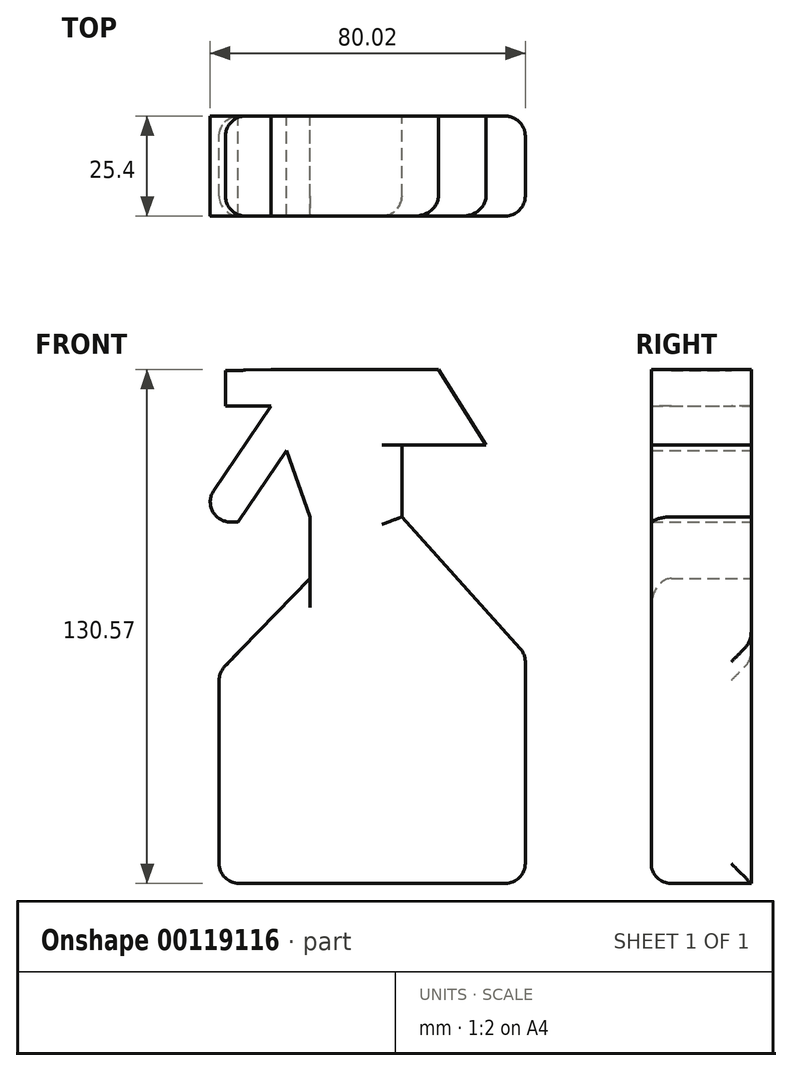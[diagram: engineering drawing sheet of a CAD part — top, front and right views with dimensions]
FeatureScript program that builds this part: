
annotation { "Feature Type Name" : "Feature", "Feature Type Description" : "" }
export const myFeature = defineFeature(function(context is Context, id is Id, definition is map)
    precondition{}
    {
        {
            var Q0;
            Q0=qCreatedBy(makeId("Front.planeOp"),FACE);
            var sketch = newSketch(context, id + "F0", { "sketchPlane" : qUnion([Q0])});
            skLineSegment(sketch, "E0", {"start": v(-54.09, 52.8) * mm, "end": v(-54.09, 43.84) * mm});
            skLineSegment(sketch, "E1", {"start": v(-54.09, 43.84) * mm, "end": v(-42.57, 43.84) * mm});
            skLineSegment(sketch, "E2", {"start": v(-42.57, 43.84) * mm, "end": v(-42.57, 53.12) * mm});
            skLineSegment(sketch, "E3", {"start": v(-54.09, 52.8) * mm, "end": v(-42.57, 53.12) * mm});
            skLineSegment(sketch, "E4", {"start": v(-42.57, 53.12) * mm, "end": v(0, 53.12) * mm});
            skLineSegment(sketch, "E5", {"start": v(0, 53.12) * mm, "end": v(12.11, 33.92) * mm});
            skLineSegment(sketch, "E6", {"start": v(12.11, 33.92) * mm, "end": v(-9.28, 33.92) * mm});
            skLineSegment(sketch, "E7", {"start": v(-9.28, 33.92) * mm, "end": v(-9.28, 15.68) * mm});
            skLineSegment(sketch, "E8", {"start": v(-9.28, 15.68) * mm, "end": v(-32.64, 15.68) * mm});
            skLineSegment(sketch, "E9", {"start": v(-32.64, 15.68) * mm, "end": v(-42.57, 43.84) * mm});
            skLineSegment(sketch, "E10", {"start": v(-42.57, 43.84) * mm, "end": v(-62.4, 14.4) * mm});
            skLineSegment(sketch, "E11", {"start": v(-62.4, 14.4) * mm, "end": v(-50.89, 14.4) * mm});
            skLineSegment(sketch, "E12", {"start": v(-50.89, 14.4) * mm, "end": v(-38.6, 32.6) * mm});
            skLineSegment(sketch, "E13", {"start": v(-32.64, 15.68) * mm, "end": v(-32.64, 0) * mm});
            skLineSegment(sketch, "E14", {"start": v(-32.64, 0) * mm, "end": v(-55.69, -23.8) * mm});
            skLineSegment(sketch, "E15", {"start": v(-55.69, -23.8) * mm, "end": v(-55.69, -77.45) * mm});
            skLineSegment(sketch, "E16", {"start": v(-55.69, -77.45) * mm, "end": v(22.08, -77.45) * mm});
            skLineSegment(sketch, "E17", {"start": v(22.08, -77.45) * mm, "end": v(22.08, -19.2) * mm});
            skLineSegment(sketch, "E18", {"start": v(-9.28, 15.68) * mm, "end": v(22.08, -19.2) * mm});
            skSolve(sketch);
        }
        {
            var Q0;
            Q0=makeQuery(id+"F0.imprint","IMPRINT",FACE,{"disambiguationData":[TD([[makeQuery(id+"F0.imprint","IMPRINT",EDGE,{"derivedFrom":sQuery(id+"F0.wireOp",EDGE,"E0")}),1.0]])]});
            var Q1;
            {var subQ0=sQuery(id+"F0.wireOp",EDGE,"E10");Q1=makeQuery(id+"F0.imprint","IMPRINT",FACE,{"disambiguationData":[TD([[makeQuery(id+"F0.imprint","IMPRINT",EDGE,{"derivedFrom":subQ0}),1.0]])]});}
            var Q2;
            Q2=makeQuery(id+"F0.imprint","IMPRINT",FACE,{"disambiguationData":[TD([[makeQuery(id+"F0.imprint","IMPRINT",EDGE,{"derivedFrom":sQuery(id+"F0.wireOp",EDGE,"E8")}),1.0]])]});
            var Q3;
            {var subQ0=sQuery(id+"F0.wireOp",EDGE,"E2");Q3=makeQuery(id+"F0.imprint","IMPRINT",FACE,{"disambiguationData":[TD([[makeQuery(id+"F0.imprint","IMPRINT",EDGE,{"derivedFrom":subQ0}),-1.0]])]});}
            extrude(context, id + "F1", {"entities" : qUnion([Q0, Q1, Q2, Q3]), "endBound" : BoundingType.SYMMETRIC, "depth" : 25.4 * mm});
        }
        {
            var Q0;
            Q0=makeQuery(id+"F1.opExtrude","CAP_EDGE",EDGE,{"disambiguationData":[OSD([sQuery(id+"F0.wireOp",EDGE,"E15")])],"isStart":false});
            var Q1;
            Q1=makeQuery(id+"F1.opExtrude","CAP_EDGE",EDGE,{"disambiguationData":[OSD([sQuery(id+"F0.wireOp",EDGE,"E14")])],"isStart":false});
            var Q2;
            Q2=makeQuery(id+"F1.opExtrude","SWEPT_EDGE",EDGE,{"disambiguationData":[OSD([sQuery(id+"F0.wireOp",EDGE,"E14"),sQuery(id+"F0.wireOp",EDGE,"E15")])]});
            var Q3;
            Q3=makeQuery(id+"F1.opExtrude","CAP_EDGE",EDGE,{"disambiguationData":[OSD([sQuery(id+"F0.wireOp",EDGE,"E15")])],"isStart":true});
            var Q4;
            Q4=makeQuery(id+"F1.opExtrude","SWEPT_EDGE",EDGE,{"disambiguationData":[OSD([sQuery(id+"F0.wireOp",EDGE,"E15"),sQuery(id+"F0.wireOp",EDGE,"E16")])]});
            var Q5;
            Q5=makeQuery(id+"F1.opExtrude","CAP_EDGE",EDGE,{"disambiguationData":[OSD([sQuery(id+"F0.wireOp",EDGE,"E16")])],"isStart":false});
            var Q6;
            Q6=makeQuery(id+"F1.opExtrude","CAP_EDGE",EDGE,{"disambiguationData":[OSD([sQuery(id+"F0.wireOp",EDGE,"E17")])],"isStart":false});
            var Q7;
            Q7=makeQuery(id+"F1.opExtrude","CAP_EDGE",EDGE,{"disambiguationData":[OSD([sQuery(id+"F0.wireOp",EDGE,"E18")])],"isStart":false});
            var Q8;
            Q8=makeQuery(id+"F1.opExtrude","CAP_EDGE",EDGE,{"disambiguationData":[OSD([sQuery(id+"F0.wireOp",EDGE,"E7")])],"isStart":false});
            var Q9;
            Q9=makeQuery(id+"F1.opExtrude","CAP_EDGE",EDGE,{"disambiguationData":[OSD([sQuery(id+"F0.wireOp",EDGE,"E5")])],"isStart":false});
            var Q10;
            Q10=makeQuery(id+"F1.opExtrude","CAP_EDGE",EDGE,{"disambiguationData":[OSD([sQuery(id+"F0.wireOp",EDGE,"E0")])],"isStart":false});
            var Q11;
            Q11=makeQuery(id+"F1.opExtrude","CAP_EDGE",EDGE,{"disambiguationData":[OSD([sQuery(id+"F0.wireOp",EDGE,"E0")])],"isStart":true});
            var Q12;
            Q12=makeQuery(id+"F1.opExtrude","SWEPT_EDGE",EDGE,{"disambiguationData":[OSD([sQuery(id+"F0.wireOp",EDGE,"E10"),sQuery(id+"F0.wireOp",EDGE,"E11")])]});
            var Q13;
            Q13=makeQuery(id+"F1.opExtrude","SWEPT_FACE",FACE,{"disambiguationData":[OSD([sQuery(id+"F0.wireOp",EDGE,"E17")])]});
            fillet(context, id + "F2", {"entities" : qUnion([Q0, Q1, Q2, Q3, Q4, Q5, Q6, Q7, Q8, Q9, Q10, Q11, Q12, Q13]), "radius" : 5.08 * mm, "tangentPropagation" : true, "allowEdgeOverflow" : false});
        }
    });
